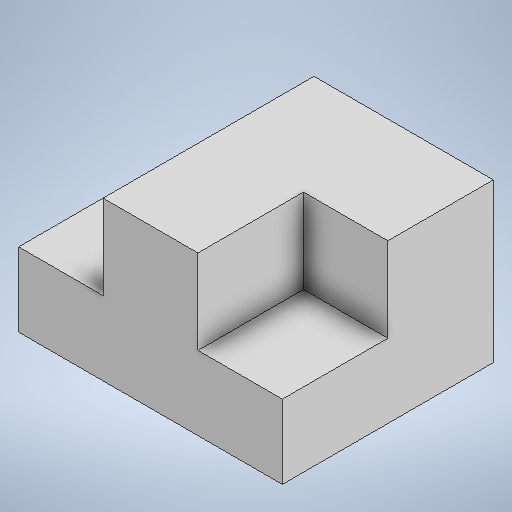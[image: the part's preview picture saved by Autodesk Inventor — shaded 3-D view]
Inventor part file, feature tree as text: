
AUTODESK INVENTOR PART (.ipt)
format: ipt  version: 2025 (Build 290162010, 162A)  size: 204,288 bytes
history: native  units: mm
features: extrude x3, sketch x2, other x1
ambient origin geometry x8: Origin, YZ Plane, XZ Plane, XY Plane, X Axis, Y Axis, Z Axis, Center Point
bodies: Body1 (feature_tree)
feature tree (6):
  other  "實體1"
  extrude  "擠出1"  Depth=25.0mm
  sketch  "草圖2"
  extrude  "擠出2"  Depth=15.0mm
  extrude  "擠出3"  Depth=20.0mm TaperAngle=0.0deg
  sketch  "草圖1"
